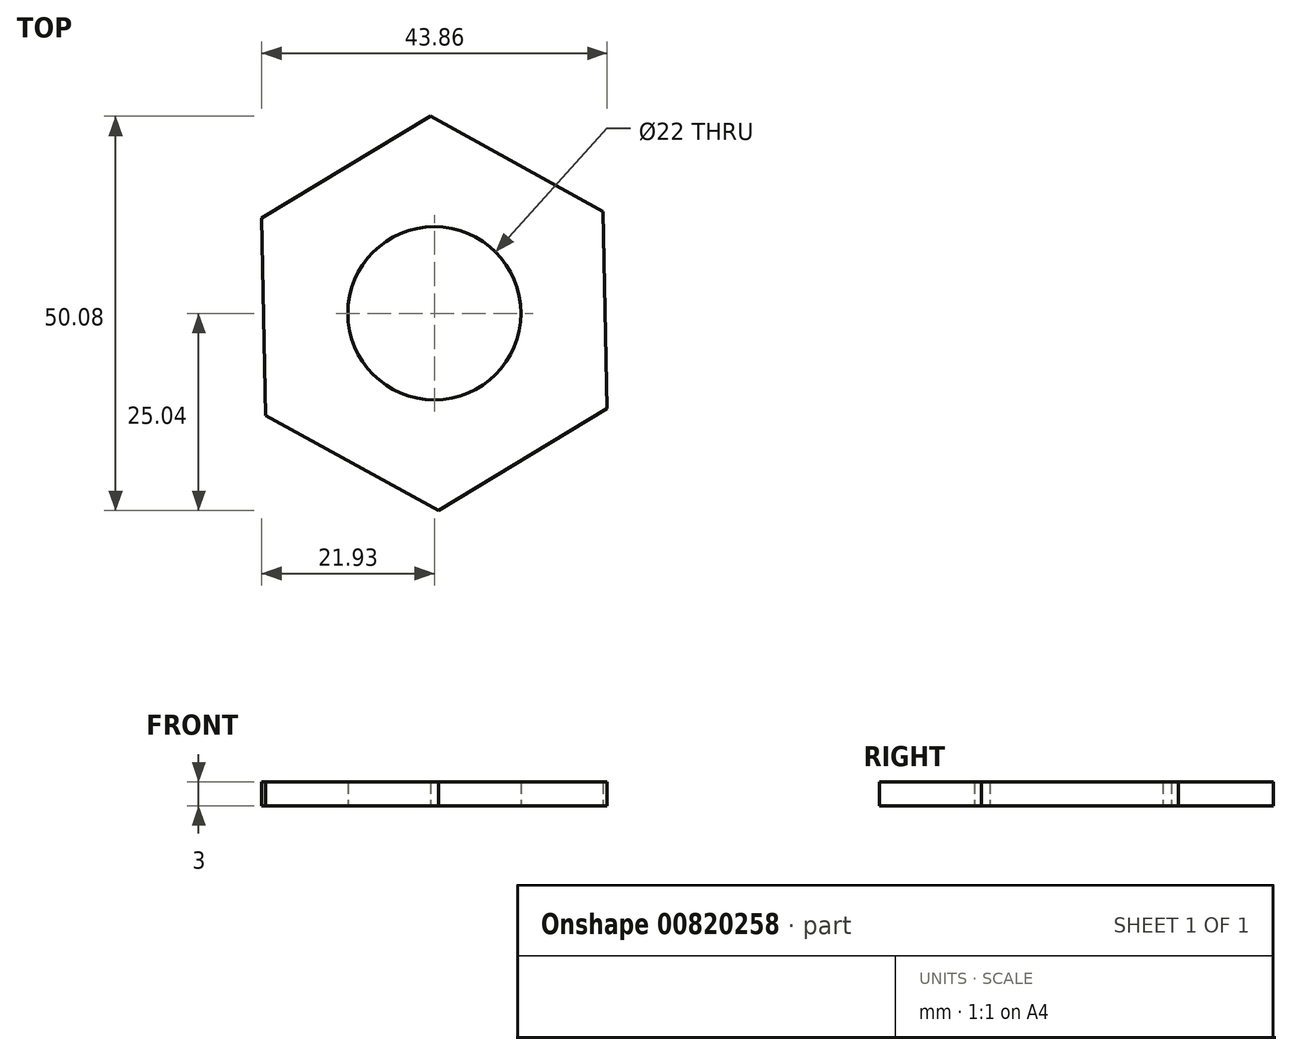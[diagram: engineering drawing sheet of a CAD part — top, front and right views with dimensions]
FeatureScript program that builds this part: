
annotation { "Feature Type Name" : "Feature", "Feature Type Description" : "" }
export const myFeature = defineFeature(function(context is Context, id is Id, definition is map)
    precondition{}
    {
        {
            var Q0;
            Q0=qCreatedBy(makeId("Top.planeOp"),FACE);
            var sketch = newSketch(context, id + "F0", { "sketchPlane" : qUnion([Q0])});
            skCircle(sketch, "E0", {"center": v(0, 0) * mm, "radius": 11 * mm});
            skLineSegment(sketch, "E1.0", {"start": v(0.5, -25.04) * mm, "end": v(-21.44, -12.95) * mm});
            skLineSegment(sketch, "E1.1", {"start": v(-21.44, -12.95) * mm, "end": v(-21.93, 12.1) * mm});
            skLineSegment(sketch, "E1.2", {"start": v(-21.93, 12.1) * mm, "end": v(-0.5, 25.04) * mm});
            skLineSegment(sketch, "E1.3", {"start": v(-0.5, 25.04) * mm, "end": v(21.44, 12.95) * mm});
            skLineSegment(sketch, "E1.4", {"start": v(21.44, 12.95) * mm, "end": v(21.93, -12.1) * mm});
            skLineSegment(sketch, "E1.5", {"start": v(21.93, -12.1) * mm, "end": v(0.5, -25.04) * mm});
            skPoint(sketch, "E1.0.midPoint", {"position": v(-10.47, -19) * mm});
            skSolve(sketch);
        }
        {
            var Q0;
            Q0=makeQuery(id+"F0.imprint","IMPRINT",FACE,{"disambiguationData":[TD([[makeQuery(id+"F0.imprint","IMPRINT",EDGE,{"derivedFrom":sQuery(id+"F0.wireOp",EDGE,"E0")}),-1.0]])]});
            extrude(context, id + "F1", {"entities" : qUnion([Q0]), "depth" : 3 * mm, "offsetDistance" : 25 * mm});
        }
    });
